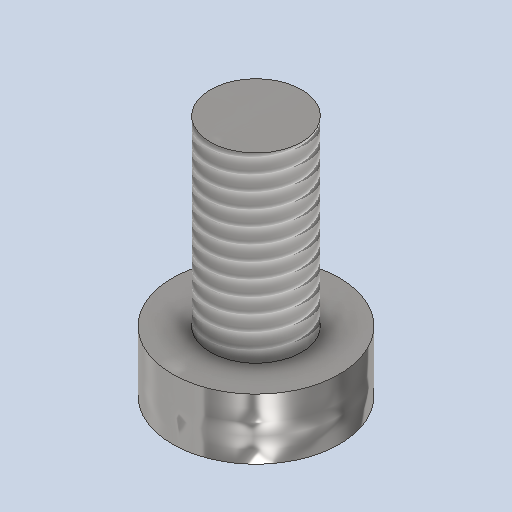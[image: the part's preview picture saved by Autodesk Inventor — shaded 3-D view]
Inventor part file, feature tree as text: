
AUTODESK INVENTOR PART (.ipt)
format: ipt  version: 2024.2 (Build 282272000, 272)  size: 182,272 bytes
history: native  units: mm
features: sketch x2, revolve x1, thread x1, extrude x1
ambient origin geometry x8: Origin, YZ Plane, XZ Plane, XY Plane, X Axis, Y Axis, Z Axis, Center Point
bodies: Solid1 (feature_tree)
feature tree (5):
  revolve  "Revolution1"  [1 undecoded]
  thread  "Thread1"  [1 undecoded]
  extrude  "Extrusion1"  [1 undecoded]
  sketch  "Sketch1"  dims[d4=90.0deg d5=6.0mm d6=0.0mm d0=0.0mm]
  sketch  "Sketch2"
note: 3 required parameter values undecoded (feature->parameter linkage not recoverable at this tier; creation-order binding heuristic only, values carry confidence <= 0.55)